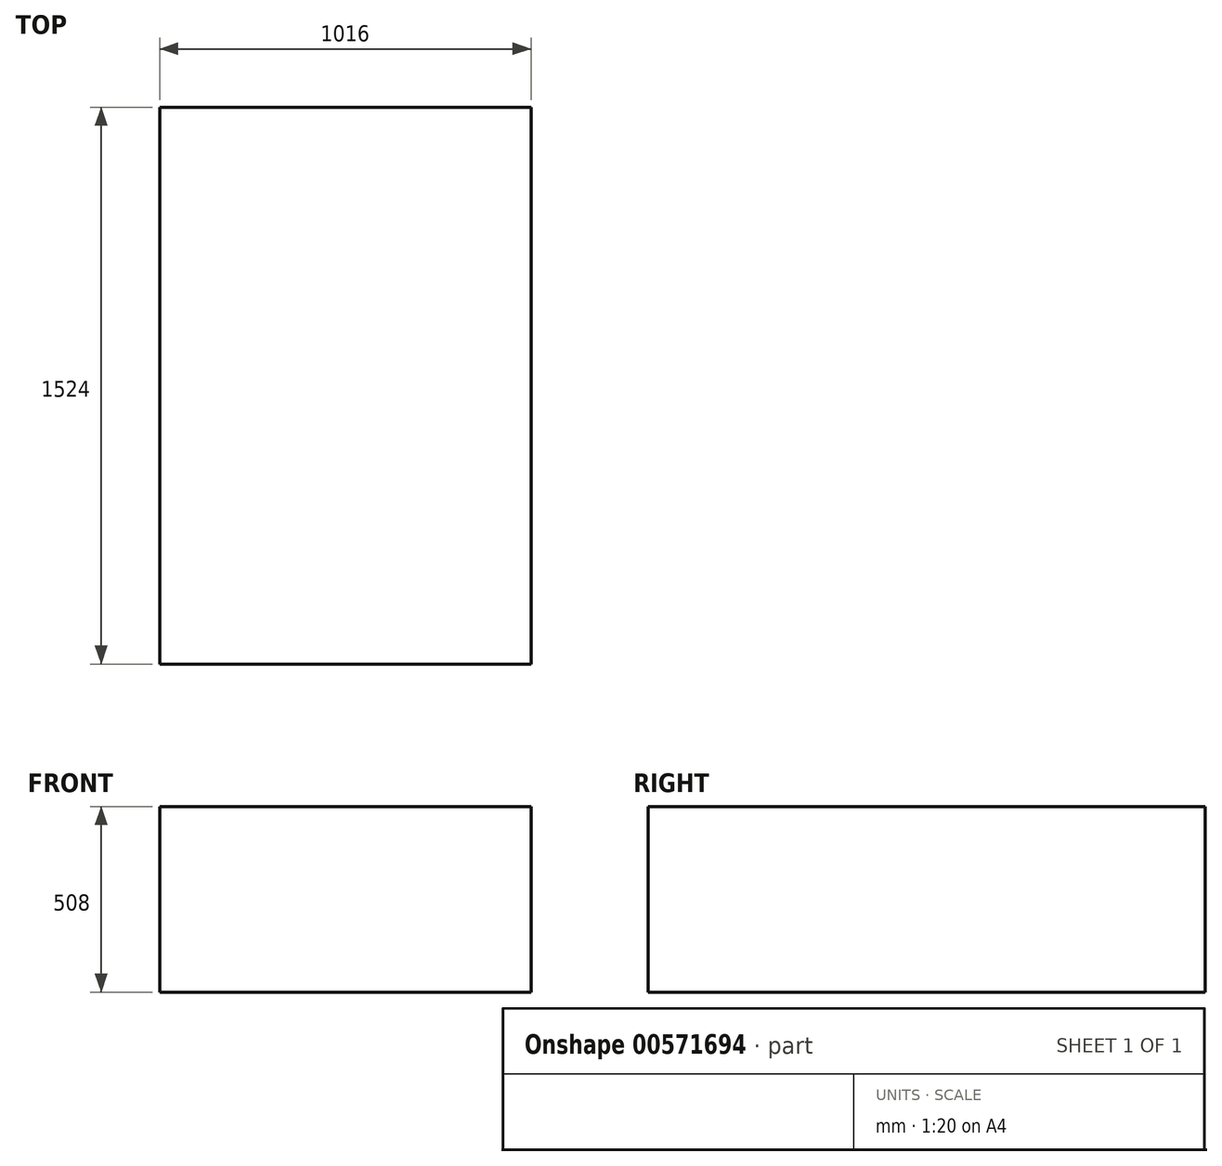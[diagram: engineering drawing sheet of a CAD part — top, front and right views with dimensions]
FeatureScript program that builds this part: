
annotation { "Feature Type Name" : "Feature", "Feature Type Description" : "" }
export const myFeature = defineFeature(function(context is Context, id is Id, definition is map)
    precondition{}
    {
        {
            var Q0;
            Q0=qCreatedBy(makeId("Top.planeOp"),FACE);
            var sketch = newSketch(context, id + "F0", { "sketchPlane" : qUnion([Q0])});
            skLineSegment(sketch, "E0.bottom", {"start": v(-508, 762) * mm, "end": v(508, 762) * mm});
            skLineSegment(sketch, "E0.top", {"start": v(-508, -762) * mm, "end": v(508, -762) * mm});
            skLineSegment(sketch, "E0.left", {"start": v(-508, 762) * mm, "end": v(-508, -762) * mm});
            skLineSegment(sketch, "E0.right", {"start": v(508, 762) * mm, "end": v(508, -762) * mm});
            skPoint(sketch, "E0.middle", {"position": v(0, 0) * mm});
            skSolve(sketch);
        }
        {
            var Q0;
            Q0=makeQuery(id+"F0.imprint","IMPRINT",FACE,{"disambiguationData":[TD([[makeQuery(id+"F0.imprint","IMPRINT",EDGE,{"derivedFrom":sQuery(id+"F0.wireOp",EDGE,"E0.bottom")}),-1.0]])]});
            extrude(context, id + "F1", {"entities" : qUnion([Q0]), "oppositeDirection" : true, "depth" : 508 * mm, "offsetDistance" : 25.4 * mm});
        }
    });
